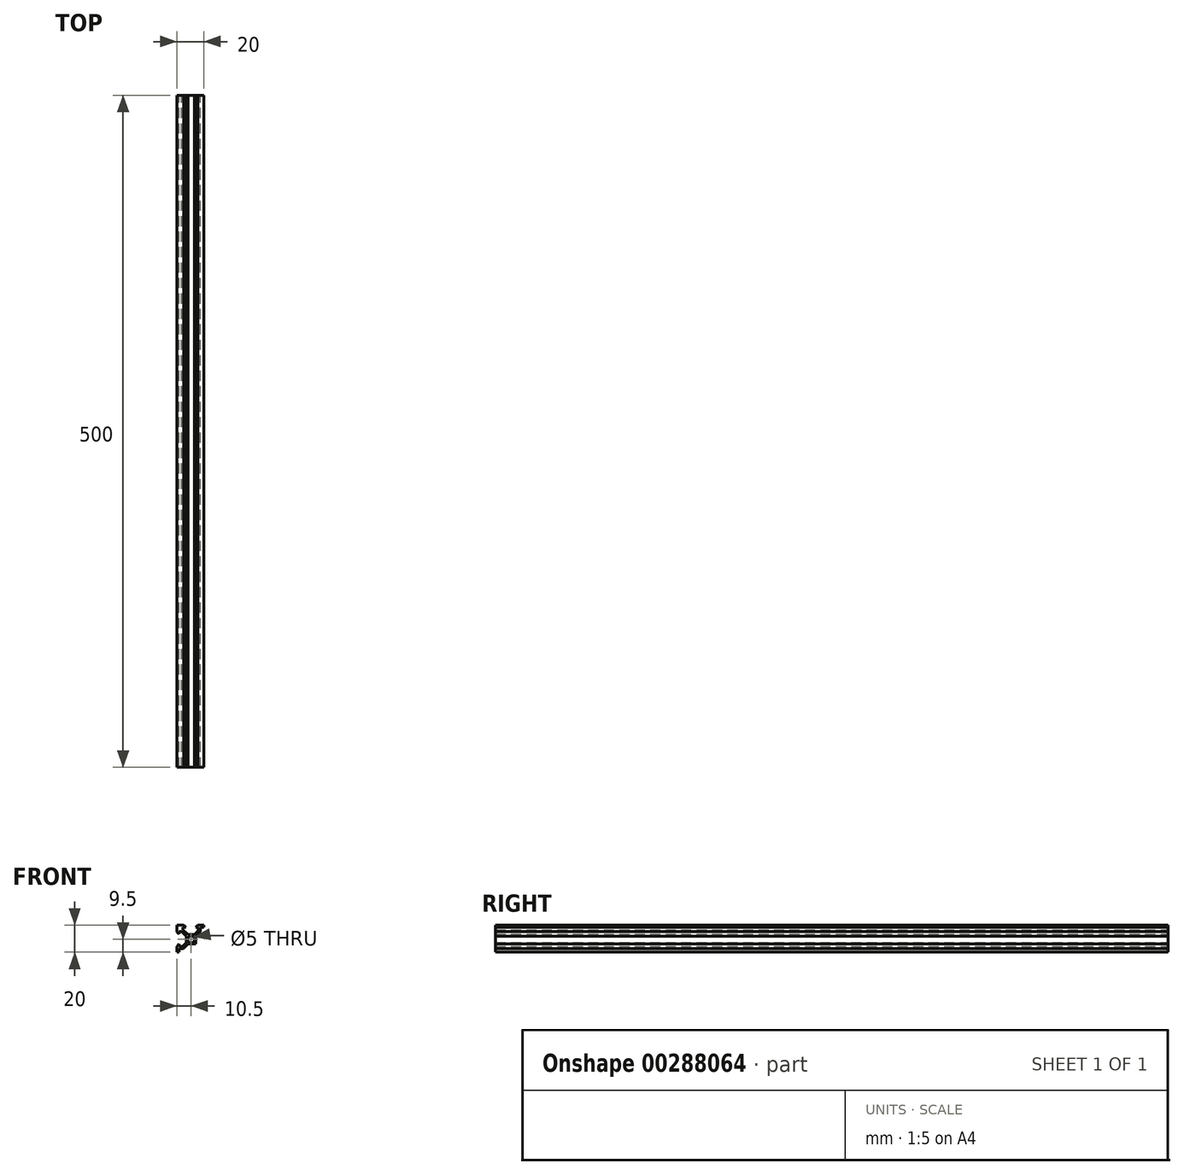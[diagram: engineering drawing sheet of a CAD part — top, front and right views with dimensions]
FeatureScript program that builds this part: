
annotation { "Feature Type Name" : "Feature", "Feature Type Description" : "" }
export const myFeature = defineFeature(function(context is Context, id is Id, definition is map)
    precondition{}
    {
        {
            var Q0;
            Q0=qCreatedBy(makeId("Front.planeOp"),FACE);
            var sketch = newSketch(context, id + "F0", { "sketchPlane" : qUnion([Q0])});
            skLineSegment(sketch, "E0.bottom", {"start": v(-6, 6) * mm, "end": v(-13, 6) * mm});
            skLineSegment(sketch, "E0.top", {"start": v(-6, 13) * mm, "end": v(-13, 13) * mm});
            skLineSegment(sketch, "E0.left", {"start": v(-6, 6) * mm, "end": v(-6, 13) * mm});
            skLineSegment(sketch, "E0.right", {"start": v(-13, 6) * mm, "end": v(-13, 13) * mm});
            skPoint(sketch, "E0.middle", {"position": v(-9.5, 9.5) * mm});
            skLineSegment(sketch, "E1", {"start": v(-13, 11.87) * mm, "end": v(-16.6, 15.47) * mm});
            skLineSegment(sketch, "E2", {"start": v(-16.6, 15.47) * mm, "end": v(-18.4, 15.47) * mm});
            skLineSegment(sketch, "E3", {"start": v(-18.4, 15.47) * mm, "end": v(-18.4, 13.4) * mm});
            skLineSegment(sketch, "E4", {"start": v(-18.4, 13.4) * mm, "end": v(-20, 15) * mm});
            skLineSegment(sketch, "E5", {"start": v(-20, 15) * mm, "end": v(-20, 20) * mm});
            skLineSegment(sketch, "E6", {"start": v(-20, 20) * mm, "end": v(-13, 13) * mm});
            skLineSegment(sketch, "E7.bottom", {"start": v(-20, 20) * mm, "end": v(20, 20) * mm});
            skLineSegment(sketch, "E7.top", {"start": v(-20, -20) * mm, "end": v(20, -20) * mm});
            skLineSegment(sketch, "E7.left", {"start": v(-20, 20) * mm, "end": v(-20, -20) * mm});
            skLineSegment(sketch, "E7.right", {"start": v(20, 20) * mm, "end": v(20, -20) * mm});
            skPoint(sketch, "E7.middle", {"position": v(0, 0) * mm});
            skLineSegment(sketch, "E8", {"start": v(-13, 7.13) * mm, "end": v(-16, 4.13) * mm});
            skLineSegment(sketch, "E9", {"start": v(-16, 4.13) * mm, "end": v(-18.4, 4.13) * mm});
            skLineSegment(sketch, "E10", {"start": v(-18.4, 4.13) * mm, "end": v(-18.4, 6) * mm});
            skLineSegment(sketch, "E11", {"start": v(-18.4, 6) * mm, "end": v(-20, 4.4) * mm});
            skLineSegment(sketch, "E12", {"start": v(-20, 4.4) * mm, "end": v(-20, 0) * mm});
            skLineSegment(sketch, "E13", {"start": v(-20, 0) * mm, "end": v(-18.4, 0) * mm});
            skLineSegment(sketch, "E14", {"start": v(-18.4, 0) * mm, "end": v(-18.4, 2.53) * mm});
            skLineSegment(sketch, "E15", {"start": v(-18.4, 2.53) * mm, "end": v(-15.34, 2.53) * mm});
            skLineSegment(sketch, "E16", {"start": v(-11.87, 6) * mm, "end": v(-15.34, 2.53) * mm});
            skCircle(sketch, "E17", {"center": v(-9.5, 9.5) * mm, "radius": 2.5 * mm});
            skLineSegment(sketch, "E18.MirrorCS", {"start": v(-7.13, 13) * mm, "end": v(-4.13, 16) * mm});
            skLineSegment(sketch, "E19.MirrorCS", {"start": v(-6, 11.87) * mm, "end": v(-2.53, 15.34) * mm});
            skLineSegment(sketch, "E20.MirrorCS", {"start": v(-2.53, 18.4) * mm, "end": v(-2.53, 15.34) * mm});
            skLineSegment(sketch, "E21.MirrorCS", {"start": v(-4.13, 16) * mm, "end": v(-4.13, 18.4) * mm});
            skLineSegment(sketch, "E22.MirrorCS", {"start": v(-6, 18.4) * mm, "end": v(-4.4, 20) * mm});
            skLineSegment(sketch, "E23.MirrorCS", {"start": v(-4.4, 20) * mm, "end": v(0, 20) * mm});
            skLineSegment(sketch, "E24.MirrorCS", {"start": v(0, 20) * mm, "end": v(0, 18.4) * mm});
            skLineSegment(sketch, "E25.MirrorCS", {"start": v(0, 18.4) * mm, "end": v(-2.53, 18.4) * mm});
            skLineSegment(sketch, "E26.MirrorCS", {"start": v(-13.4, 18.4) * mm, "end": v(-15, 20) * mm});
            skLineSegment(sketch, "E27.MirrorCS", {"start": v(-15.47, 18.4) * mm, "end": v(-13.4, 18.4) * mm});
            skLineSegment(sketch, "E28.MirrorCS", {"start": v(-11.87, 13) * mm, "end": v(-15.47, 16.6) * mm});
            skLineSegment(sketch, "E29.MirrorCS", {"start": v(-15.47, 16.6) * mm, "end": v(-15.47, 18.4) * mm});
            skLineSegment(sketch, "E30.MirrorCS", {"start": v(-4.13, 18.4) * mm, "end": v(-6, 18.4) * mm});
            skLineSegment(sketch, "E31", {"start": v(0, 0) * mm, "end": v(-20, 20) * mm});
            skLineSegment(sketch, "E32", {"start": v(0, 24.8) * mm, "end": v(0, -25.08) * mm});
            skPoint(sketch, "E32.endSnap0", {"position": v(0, -20) * mm});
            skLineSegment(sketch, "E33", {"start": v(-31.6, 0) * mm, "end": v(31, 0) * mm});
            skSolve(sketch);
        }
        {
            var Q0;
            {var subQ0=sQuery(id+"F0.wireOp",EDGE,"E1");Q0=makeQuery(id+"F0.imprint","IMPRINT",FACE,{"disambiguationData":[TD([[makeQuery(id+"F0.imprint","IMPRINT",EDGE,{"derivedFrom":subQ0}),-1.0]])]});}
            var Q1;
            {var subQ3=sQuery(id+"F0.wireOp",EDGE,"E26.MirrorCS");Q1=makeQuery(id+"F0.imprint","IMPRINT",FACE,{"disambiguationData":[TD([[makeQuery(id+"F0.imprint","IMPRINT",EDGE,{"derivedFrom":subQ3}),1.0]])]});}
            var Q2;
            {var subQ6=sQuery(id+"F0.wireOp",EDGE,"E8");Q2=makeQuery(id+"F0.imprint","IMPRINT",FACE,{"disambiguationData":[TD([[makeQuery(id+"F0.imprint","IMPRINT",EDGE,{"derivedFrom":subQ6}),1.0]])]});}
            var Q3;
            {var subQ0=sQuery(id+"F0.wireOp",EDGE,"E0.right");var subQ1=sQuery(id+"F0.wireOp",EDGE,"E0.bottom");var subQ2=makeQuery(id+"F0.imprint","INTERSECT",VERTEX,{"derivedFrom":[subQ1,subQ0]});Q3=makeQuery(id+"F0.imprint","IMPRINT",FACE,{"disambiguationData":[TD([[makeQuery(id+"F0.imprint","IMPRINT",EDGE,{"disambiguationData":[TD([[subQ2,1.0]])],"derivedFrom":subQ1}),-1.0]])]});}
            var Q4;
            {var subQ0=sQuery(id+"F0.wireOp",EDGE,"E0.top");var subQ1=sQuery(id+"F0.wireOp",EDGE,"E0.left");var subQ2=makeQuery(id+"F0.imprint","INTERSECT",VERTEX,{"derivedFrom":[subQ1,subQ0]});Q4=makeQuery(id+"F0.imprint","IMPRINT",FACE,{"disambiguationData":[TD([[makeQuery(id+"F0.imprint","IMPRINT",EDGE,{"disambiguationData":[TD([[subQ2,1.0]])],"derivedFrom":subQ1}),1.0]])]});}
            var Q5;
            {var subQ9=sQuery(id+"F0.wireOp",EDGE,"E18.MirrorCS");Q5=makeQuery(id+"F0.imprint","IMPRINT",FACE,{"disambiguationData":[TD([[makeQuery(id+"F0.imprint","IMPRINT",EDGE,{"derivedFrom":subQ9}),-1.0]])]});}
            extrude(context, id + "F1", {"entities" : qUnion([Q0, Q1, Q2, Q3, Q4, Q5]), "depth" : 500 * mm});
        }
    });
